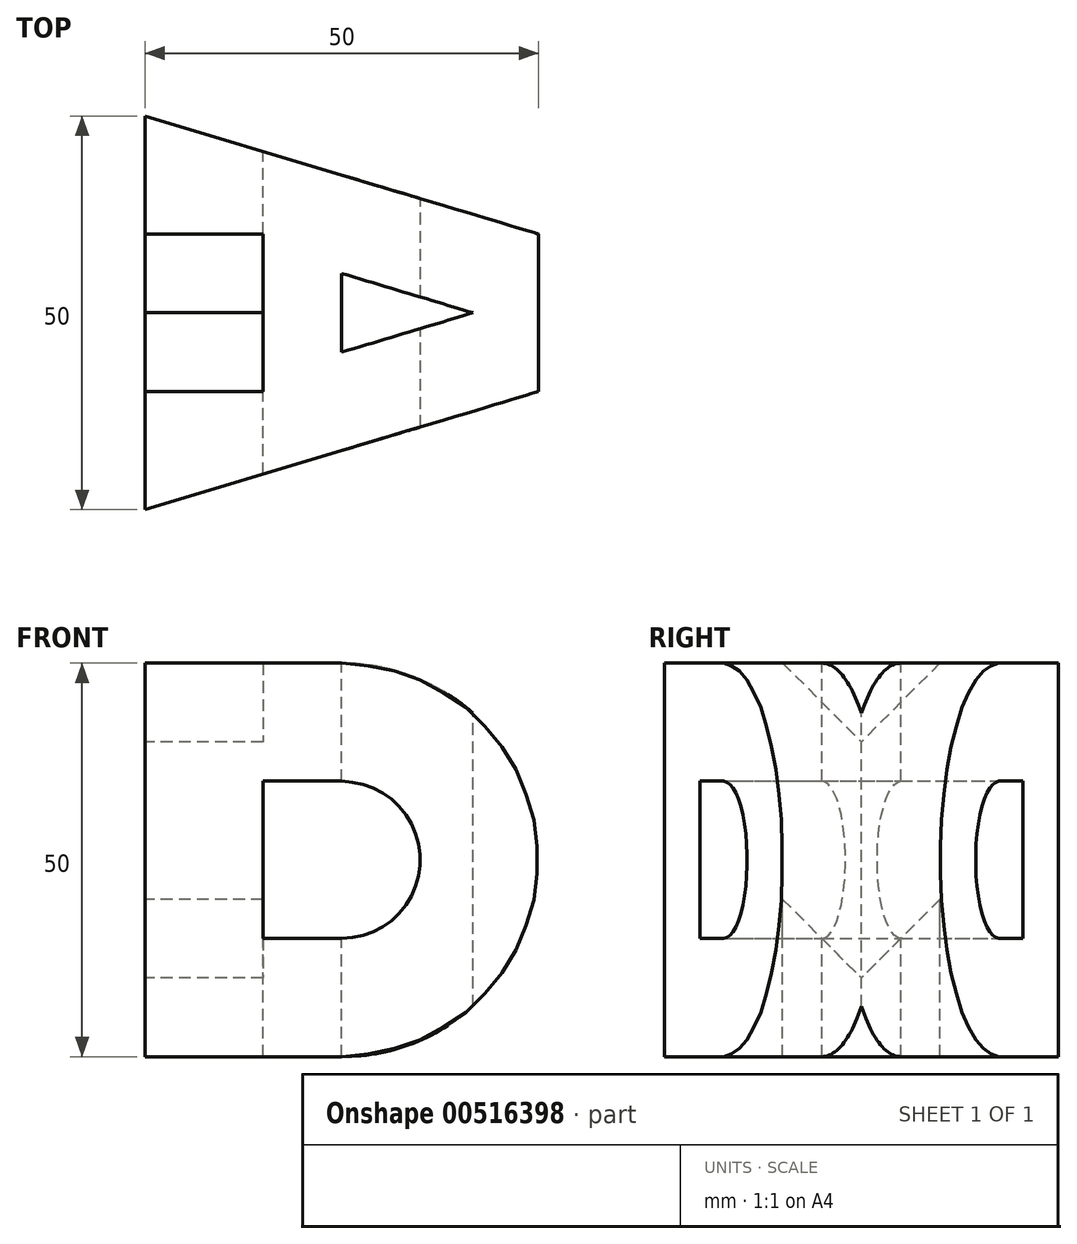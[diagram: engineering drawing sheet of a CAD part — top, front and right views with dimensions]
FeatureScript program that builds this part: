
annotation { "Feature Type Name" : "Feature", "Feature Type Description" : "" }
export const myFeature = defineFeature(function(context is Context, id is Id, definition is map)
    precondition{}
    {
        {
            var Q0;
            Q0=qCreatedBy(makeId("Front.planeOp"),FACE);
            var sketch = newSketch(context, id + "F0", { "sketchPlane" : qUnion([Q0])});
            skLineSegment(sketch, "E0", {"start": v(0, 50) * mm, "end": v(0, 0) * mm});
            skLineSegment(sketch, "E1", {"start": v(0, 50) * mm, "end": v(25, 50) * mm});
            skLineSegment(sketch, "E2", {"start": v(0, 0) * mm, "end": v(25, 0) * mm});
            skArc(sketch, "E3", {"start": v(25, 50) * mm, "mid": v(42.68, 42.68) * mm, "end": v(50, 25) * mm});
            skArc(sketch, "E4", {"start": v(25, 0) * mm, "mid": v(42.68, 7.32) * mm, "end": v(50, 25) * mm});
            skLineSegment(sketch, "E5", {"start": v(0, 50) * mm, "end": v(15, 50) * mm, "construction": true});
            skLineSegment(sketch, "E6", {"start": v(15, 15) * mm, "end": v(25, 15) * mm});
            skArc(sketch, "E7", {"start": v(25, 15) * mm, "mid": v(32.07, 17.93) * mm, "end": v(35, 25) * mm});
            skLineSegment(sketch, "E8.MirrorCS", {"start": v(15, 35) * mm, "end": v(25, 35) * mm});
            skArc(sketch, "E9.MirrorCS", {"start": v(25, 35) * mm, "mid": v(32.07, 32.07) * mm, "end": v(35, 25) * mm});
            skLineSegment(sketch, "E10", {"start": v(15, 15) * mm, "end": v(15, 35) * mm});
            skSolve(sketch);
        }
        {
            var Q0;
            Q0=makeQuery(id+"F0.imprint","IMPRINT",FACE,{"disambiguationData":[TD([[makeQuery(id+"F0.imprint","IMPRINT",EDGE,{"derivedFrom":sQuery(id+"F0.wireOp",EDGE,"E0")}),1.0]])]});
            extrude(context, id + "F1", {"entities" : qUnion([Q0]), "depth" : 50 * mm, "offsetDistance" : 25 * mm});
        }
        {
            var Q0;
            Q0=makeQuery(id+"F1.opExtrude","SWEPT_FACE",FACE,{"disambiguationData":[OSD([sQuery(id+"F0.wireOp",EDGE,"E0")])]});
            var sketch = newSketch(context, id + "F2", { "sketchPlane" : qUnion([Q0])});
            skLineSegment(sketch, "E11", {"start": v(0, 50) * mm, "end": v(15, 50) * mm});
            skLineSegment(sketch, "E12", {"start": v(50, 50) * mm, "end": v(35, 50) * mm});
            skLineSegment(sketch, "E13", {"start": v(0, 0) * mm, "end": v(15, 0) * mm});
            skLineSegment(sketch, "E14", {"start": v(50, 0) * mm, "end": v(35, 0) * mm});
            skLineSegment(sketch, "E15", {"start": v(15, 50) * mm, "end": v(25, 40) * mm});
            skLineSegment(sketch, "E16", {"start": v(35, 50) * mm, "end": v(25, 40) * mm});
            skPoint(sketch, "E17", {"position": v(25, 40) * mm});
            skLineSegment(sketch, "E18", {"start": v(15, 50) * mm, "end": v(35, 50) * mm});
            skLineSegment(sketch, "E19", {"start": v(15, 0) * mm, "end": v(15, 20) * mm});
            skLineSegment(sketch, "E20", {"start": v(35, 0) * mm, "end": v(35, 20) * mm});
            skLineSegment(sketch, "E21", {"start": v(35, 20) * mm, "end": v(25, 10) * mm});
            skLineSegment(sketch, "E22", {"start": v(15, 20) * mm, "end": v(25, 10) * mm});
            skPoint(sketch, "E23", {"position": v(25, 10) * mm});
            skLineSegment(sketch, "E24", {"start": v(15, 0) * mm, "end": v(35, 0) * mm});
            skSolve(sketch);
        }
        {
            var Q0;
            Q0=makeQuery(id+"F2.imprint","IMPRINT",FACE,{"disambiguationData":[TD([[makeQuery(id+"F2.imprint","IMPRINT",EDGE,{"derivedFrom":sQuery(id+"F2.wireOp",EDGE,"E19")}),-1.0]])]});
            var Q1;
            Q1=makeQuery(id+"F2.imprint","IMPRINT",FACE,{"disambiguationData":[TD([[makeQuery(id+"F2.imprint","IMPRINT",EDGE,{"derivedFrom":sQuery(id+"F2.wireOp",EDGE,"E15")}),1.0]])]});
            extrude(context, id + "F3", {"entities" : qUnion([Q0, Q1]), "operationType" : NewBodyOperationType.REMOVE, "oppositeDirection" : true, "depth" : 15 * mm, "offsetDistance" : 25 * mm});
        }
        {
            var Q0;
            {var subQ3=sQuery(id+"F0.wireOp",EDGE,"E1");Q0=makeQuery(id+"F3.boolean.opBoolean","SPLIT",FACE,{"disambiguationData":[TD([makeQuery(id+"F3.opExtrude","SWEPT_FACE",FACE,{"disambiguationData":[OSD([sQuery(id+"F2.wireOp",EDGE,"E16")])]})])],"derivedFrom":makeQuery(id+"F1.opExtrude","SWEPT_FACE",FACE,{"disambiguationData":[OSD([subQ3])]})});}
            cPlane(context, id + "F4", {"entities" : qUnion([Q0]), "cplaneType" : CPlaneType.OFFSET, "offset" : 0 * mm, "width" : 150 * mm, "height" : 150 * mm});
        }
        {
            var Q0;
            Q0=qCreatedBy(id+"F4.planeOp",FACE);
            var sketch = newSketch(context, id + "F5", { "sketchPlane" : qUnion([Q0])});
            skLineSegment(sketch, "E25", {"start": v(0, 0) * mm, "end": v(50, 0) * mm, "construction": true});
            skLineSegment(sketch, "E26", {"start": v(0, -50) * mm, "end": v(0, 0) * mm, "construction": true});
            skLineSegment(sketch, "E27", {"start": v(0, -50) * mm, "end": v(50, -50) * mm, "construction": true});
            skLineSegment(sketch, "E28", {"start": v(50, -35) * mm, "end": v(50, -15) * mm, "construction": true});
            skLineSegment(sketch, "E29", {"start": v(50, -35) * mm, "end": v(50, -15) * mm});
            skLineSegment(sketch, "E30", {"start": v(50, -35) * mm, "end": v(50, -50) * mm, "construction": true});
            skLineSegment(sketch, "E31", {"start": v(50, -35) * mm, "end": v(0, -50) * mm});
            skLineSegment(sketch, "E32", {"start": v(50, -15) * mm, "end": v(0, 0) * mm});
            skLineSegment(sketch, "E33", {"start": v(25, 0) * mm, "end": v(25, -20) * mm, "construction": true});
            skLineSegment(sketch, "E34.trimOffspring", {"start": v(25, -30) * mm, "end": v(25, -50) * mm, "construction": true});
            skPoint(sketch, "E35.start.orphan", {"position": v(25, -25) * mm});
            skLineSegment(sketch, "E36", {"start": v(25, -20) * mm, "end": v(25, -30) * mm});
            skLineSegment(sketch, "E37", {"start": v(50, 0) * mm, "end": v(50, -15) * mm});
            skLineSegment(sketch, "E38", {"start": v(50, 0) * mm, "end": v(0, 0) * mm});
            skLineSegment(sketch, "E39", {"start": v(0, -50) * mm, "end": v(50, -50) * mm});
            skLineSegment(sketch, "E40", {"start": v(50, -50) * mm, "end": v(50, -35) * mm});
            skLineSegment(sketch, "E41", {"start": v(50, -15) * mm, "end": v(75, -15) * mm, "construction": true});
            skLineSegment(sketch, "E42", {"start": v(50, -35) * mm, "end": v(75, -35) * mm, "construction": true});
            skLineSegment(sketch, "E43", {"start": v(25, -20) * mm, "end": v(41.67, -25) * mm});
            skLineSegment(sketch, "E44", {"start": v(25, -30) * mm, "end": v(41.67, -25) * mm});
            skPoint(sketch, "E45", {"position": v(41.67, -25) * mm});
            skSolve(sketch);
        }
        {
            var Q0;
            Q0=makeQuery(id+"F5.imprint","IMPRINT",FACE,{"disambiguationData":[TD([[makeQuery(id+"F5.imprint","IMPRINT",EDGE,{"derivedFrom":sQuery(id+"F5.wireOp",EDGE,"E36")}),1.0]])]});
            var Q1;
            Q1=makeQuery(id+"F5.imprint","IMPRINT",FACE,{"disambiguationData":[TD([[makeQuery(id+"F5.imprint","IMPRINT",EDGE,{"derivedFrom":sQuery(id+"F5.wireOp",EDGE,"E31")}),1.0]])]});
            var Q2;
            Q2=makeQuery(id+"F5.imprint","IMPRINT",FACE,{"disambiguationData":[TD([[makeQuery(id+"F5.imprint","IMPRINT",EDGE,{"derivedFrom":sQuery(id+"F5.wireOp",EDGE,"E32")}),-1.0]])]});
            extrude(context, id + "F6", {"entities" : qUnion([Q0, Q1, Q2]), "operationType" : NewBodyOperationType.REMOVE, "oppositeDirection" : true, "depth" : 50 * mm, "offsetDistance" : 25 * mm});
        }
    });
